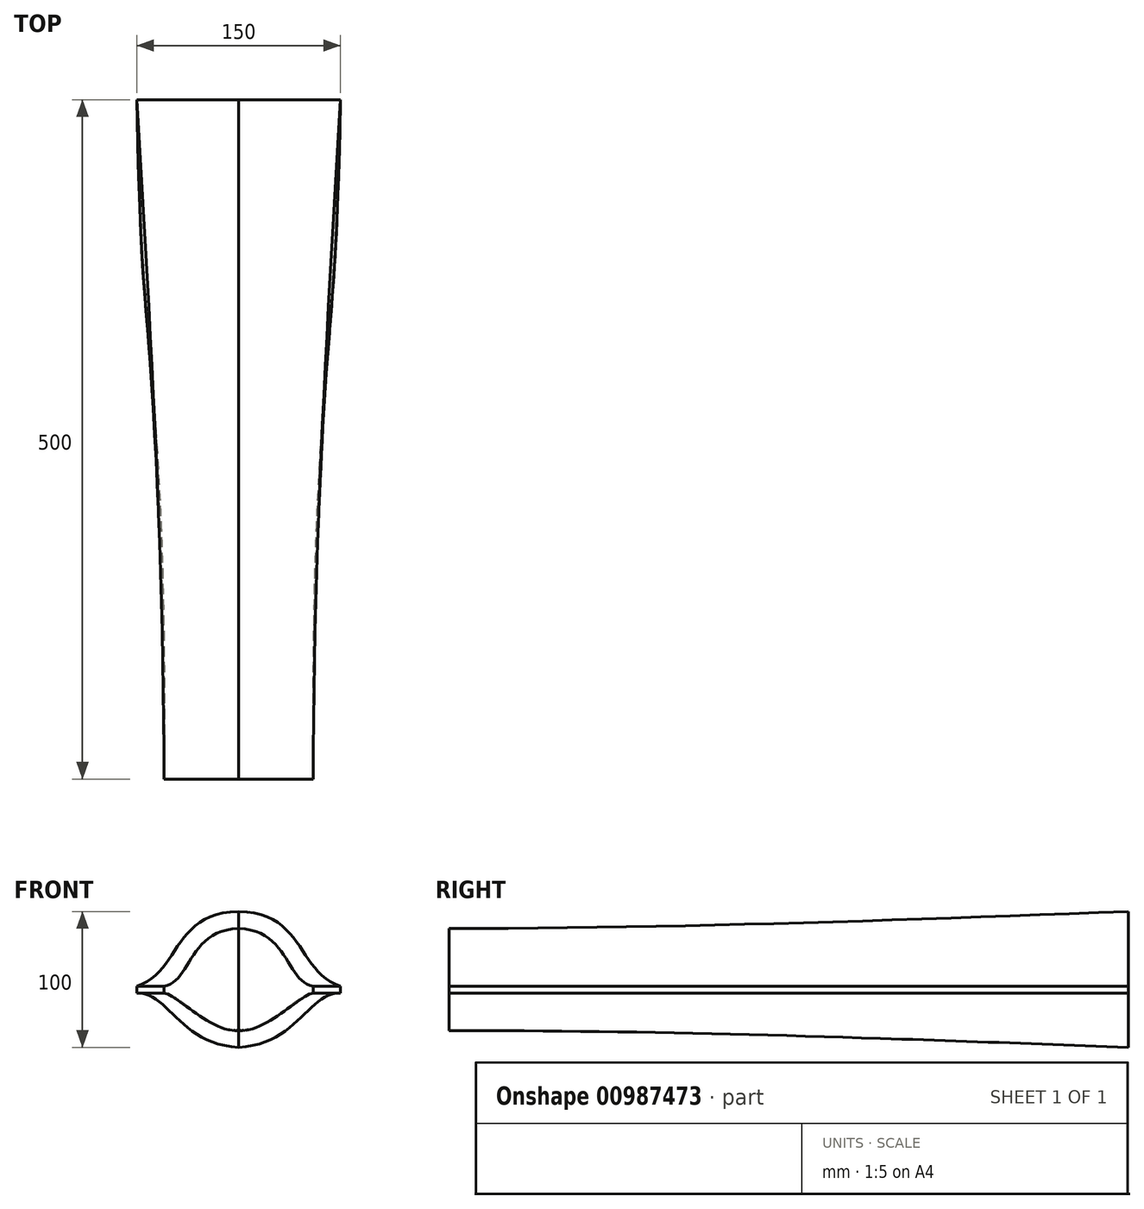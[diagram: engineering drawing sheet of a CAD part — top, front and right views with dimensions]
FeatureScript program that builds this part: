
annotation { "Feature Type Name" : "Feature", "Feature Type Description" : "" }
export const myFeature = defineFeature(function(context is Context, id is Id, definition is map)
    precondition{}
    {
        {
            var Q0;
            Q0=qCreatedBy(makeId("Front.planeOp"),FACE);
            var sketch = newSketch(context, id + "F0", { "sketchPlane" : qUnion([Q0])});
            skCircle(sketch, "E0", {"center": v(0, 0) * mm, "radius": 50 * mm, "construction": true});
            skFitSpline(sketch, "E1", {"points": [v(0, 50) * mm, v(-75, -5) * mm], "startDerivative": vector(-146.78, -2.94) * mm, "endDerivative": vector(-96.11, -31.22) * mm});
            skFitSpline(sketch, "E2", {"points": [v(-75, -10) * mm, v(0, -50) * mm], "startDerivative": vector(71.5, 0.36) * mm, "endDerivative": vector(128.89, -6.3) * mm});
            skLineSegment(sketch, "E3", {"start": v(-75, -5) * mm, "end": v(-75, -10) * mm});
            skLineSegment(sketch, "E4", {"start": v(0, -50) * mm, "end": v(0, 50) * mm});
            skSolve(sketch);
        }
        {
            var Q0;
            Q0=qCreatedBy(makeId("Front.planeOp"),FACE);
            cPlane(context, id + "F1", {"entities" : qUnion([Q0]), "cplaneType" : CPlaneType.OFFSET, "offset" : 500 * mm, "width" : 150 * mm, "height" : 150 * mm});
        }
        {
            var Q0;
            Q0=qCreatedBy(id+"F1.planeOp",FACE);
            var sketch = newSketch(context, id + "F2", { "sketchPlane" : qUnion([Q0])});
            skCircle(sketch, "E5", {"center": v(0, 0) * mm, "radius": 37.5 * mm, "construction": true});
            skPoint(sketch, "E6.0", {"position": v(-75, -5) * mm});
            skPoint(sketch, "E7.0", {"position": v(-75, -10) * mm});
            skPoint(sketch, "E8.0", {"position": v(0, 50) * mm});
            skLineSegment(sketch, "E9", {"start": v(-75, -10) * mm, "end": v(0, -10) * mm, "construction": true});
            skLineSegment(sketch, "E10", {"start": v(-75, -5) * mm, "end": v(0, -5) * mm, "construction": true});
            skFitSpline(sketch, "E11", {"points": [v(-55, -5) * mm, v(0, 37.5) * mm], "startDerivative": vector(60.1, 8.06) * mm, "endDerivative": vector(112.02, 3.59) * mm});
            skFitSpline(sketch, "E12", {"points": [v(0, -37.5) * mm, v(-55, -10) * mm], "startDerivative": vector(-61.9, -5.73) * mm, "endDerivative": vector(-30.6, 3.78) * mm});
            skLineSegment(sketch, "E13", {"start": v(0, 37.5) * mm, "end": v(0, -37.5) * mm});
            skLineSegment(sketch, "E14", {"start": v(-55, -5) * mm, "end": v(-55, -10) * mm});
            skSolve(sketch);
        }
        {
            var Q0;
            Q0=sQuery(id+"F0.wireOp",VERTEX,"E2.start");
            var Q1;
            Q1=sQuery(id+"F2.wireOp",VERTEX,"E12.end");
            var Q2;
            Q2=sQuery(id+"F2.wireOp",VERTEX,"E9.end");
            cPlane(context, id + "F3", {"entities" : qUnion([Q0, Q1, Q2]), "cplaneType" : CPlaneType.THREE_POINT, "offset" : 25 * mm, "width" : 150 * mm, "height" : 150 * mm});
        }
        {
            var Q0;
            Q0=qCreatedBy(id+"F3.planeOp",FACE);
            var sketch = newSketch(context, id + "F4", { "sketchPlane" : qUnion([Q0])});
            skLineSegment(sketch, "E15", {"start": v(0, 0) * mm, "end": v(0, 500) * mm, "construction": true});
            skLineSegment(sketch, "E16", {"start": v(0, 250) * mm, "end": v(-134.27, 250) * mm, "construction": true});
            skLineSegment(sketch, "E17", {"start": v(-134.27, 250) * mm, "end": v(-134.27, 166.67) * mm, "construction": true});
            skLineSegment(sketch, "E18", {"start": v(-134.27, 166.67) * mm, "end": v(0, 166.67) * mm, "construction": true});
            skPoint(sketch, "E19.0", {"position": v(0, 500) * mm});
            skPoint(sketch, "E20.0", {"position": v(-75, 0) * mm});
            skPoint(sketch, "E21.0", {"position": v(-55, 500) * mm});
            skFitSpline(sketch, "E22", {"points": [v(-75, 0) * mm, v(-67.14, 166.67) * mm, v(-55, 500) * mm], "startDerivative": vector(15.02, 690.94) * mm, "endDerivative": vector(-11.55, 918.8) * mm});
            skSolve(sketch);
        }
        {
            var Q0;
            Q0=sQuery(id+"F4.wireOp",EDGE,"E22");
            var Q1;
            Q1=makeQuery(id+"F2.imprint","IMPRINT",FACE,{"disambiguationData":[TD([[makeQuery(id+"F2.imprint","IMPRINT",EDGE,{"derivedFrom":sQuery(id+"F2.wireOp",EDGE,"E11")}),-1.0]])]});
            var Q2;
            Q2=makeQuery(id+"F0.imprint","IMPRINT",FACE,{"disambiguationData":[TD([[makeQuery(id+"F0.imprint","IMPRINT",EDGE,{"derivedFrom":sQuery(id+"F0.wireOp",EDGE,"E1")}),1.0]])]});
            var Q3;
            Q3=sQuery(id+"F4.wireOp",EDGE,"E22");
            loft(context, id + "F5", {"spine" : qUnion([Q0]), "addGuides" : true, "startCondition" : LoftEndDerivativeType.NORMAL_TO_PROFILE, "startMagnitude" : 1, "sheetProfilesArray" : [{ "sheetProfileEntities" : qUnion([Q1]) }, { "sheetProfileEntities" : qUnion([Q2]) }], "guidesArray" : [{ "guideEntities" : qUnion([Q3]), "guideDerivativeType" : LoftGuideDerivativeType.DEFAULT, "guideDerivativeMagnitude" : 1 }]});
        }
        {
            var Q0;
            Q0=makeQuery(id+"F5.opLoft","SWEPT_BODY",BODY,{"disambiguationData":[OSD([makeQuery(id+"F0.imprint","IMPRINT",FACE,{"disambiguationData":[TD([[makeQuery(id+"F0.imprint","IMPRINT",EDGE,{"derivedFrom":sQuery(id+"F0.wireOp",EDGE,"E1")}),1.0]])]}),makeQuery(id+"F2.imprint","IMPRINT",FACE,{"disambiguationData":[TD([[makeQuery(id+"F2.imprint","IMPRINT",EDGE,{"derivedFrom":sQuery(id+"F2.wireOp",EDGE,"E11")}),-1.0]])]}),sQuery(id+"F4.wireOp",EDGE,"E22")])]});
            var Q1;
            Q1=qCreatedBy(makeId("Right.planeOp"),FACE);
            mirror(context, id + "F6", {"entities" : qUnion([Q0]), "mirrorPlane" : qUnion([Q1])});
        }
    });
